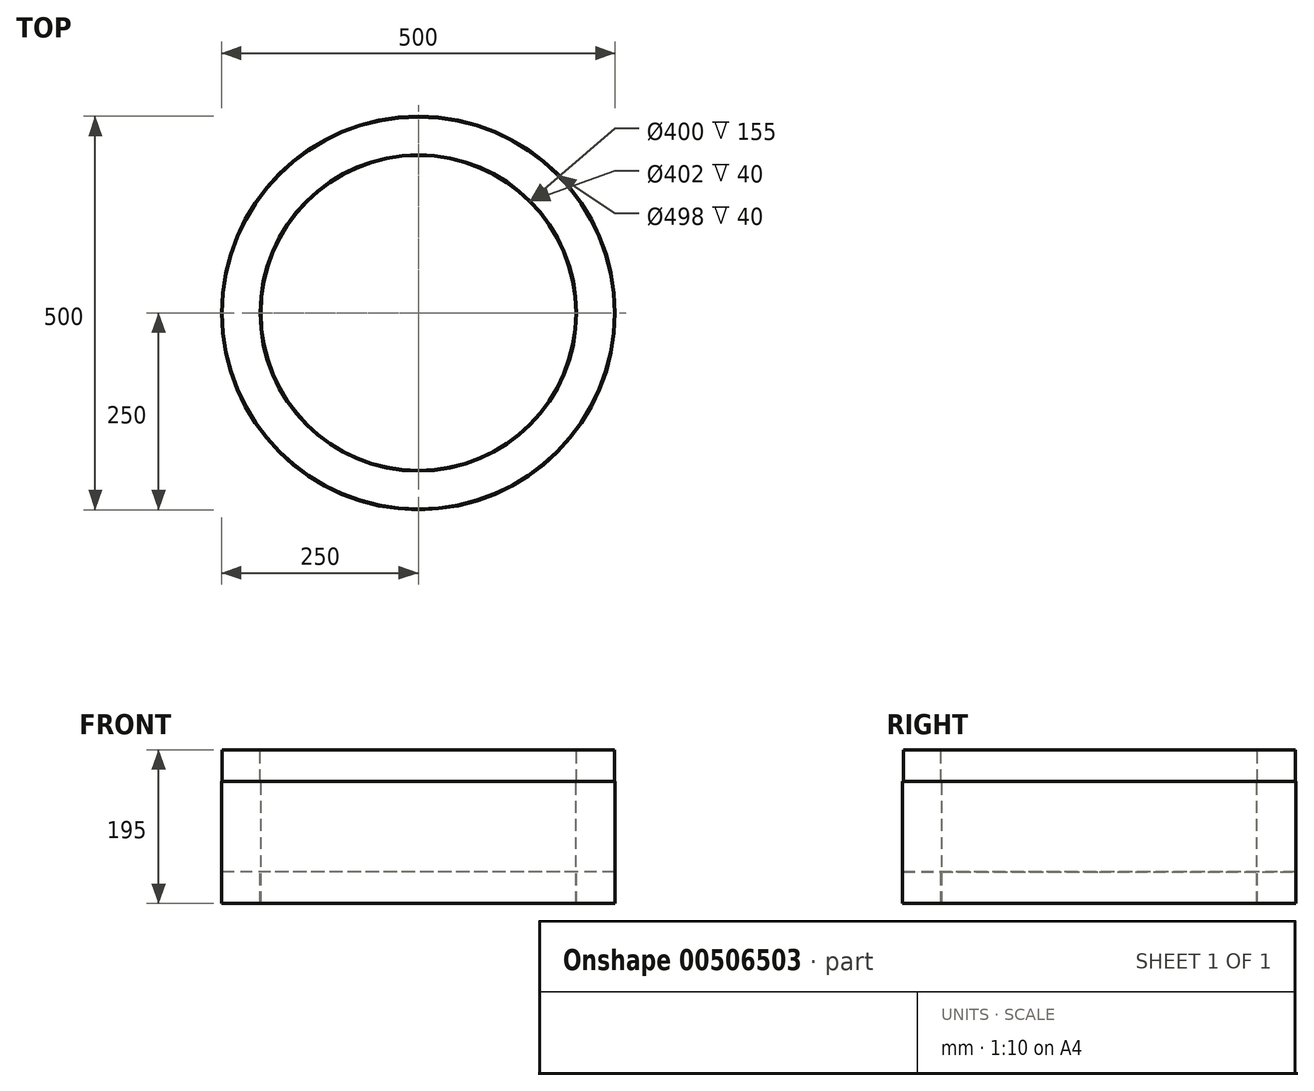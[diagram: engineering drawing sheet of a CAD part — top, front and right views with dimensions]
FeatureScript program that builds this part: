
annotation { "Feature Type Name" : "Feature", "Feature Type Description" : "" }
export const myFeature = defineFeature(function(context is Context, id is Id, definition is map)
    precondition{}
    {
        {
            var Q0;
            Q0=qCreatedBy(makeId("Front.planeOp"),FACE);
            var sketch = newSketch(context, id + "F0", { "sketchPlane" : qUnion([Q0])});
            skLineSegment(sketch, "E0", {"start": v(0, 74.87) * mm, "end": v(0, -73.71) * mm, "construction": true});
            skLineSegment(sketch, "E1", {"start": v(0, 374.84) * mm, "end": v(0, -528.94) * mm, "construction": true});
            skLineSegment(sketch, "E2", {"start": v(-200, -489.75) * mm, "end": v(-200, -334.75) * mm});
            skLineSegment(sketch, "E3", {"start": v(-200, -334.75) * mm, "end": v(-201, -334.75) * mm});
            skLineSegment(sketch, "E4", {"start": v(-201, -334.75) * mm, "end": v(-201, -294.75) * mm});
            skLineSegment(sketch, "E5", {"start": v(-201, -294.75) * mm, "end": v(-249, -294.75) * mm});
            skLineSegment(sketch, "E6", {"start": v(-249, -294.75) * mm, "end": v(-249, -334.75) * mm});
            skLineSegment(sketch, "E7", {"start": v(-249, -334.75) * mm, "end": v(-250, -334.75) * mm});
            skLineSegment(sketch, "E8", {"start": v(-250, -334.75) * mm, "end": v(-250, -489.75) * mm});
            skLineSegment(sketch, "E9", {"start": v(-250, -489.75) * mm, "end": v(-249, -489.75) * mm});
            skLineSegment(sketch, "E10", {"start": v(-249, -489.75) * mm, "end": v(-249, -449.75) * mm});
            skLineSegment(sketch, "E11", {"start": v(-249, -449.75) * mm, "end": v(-201, -449.75) * mm});
            skLineSegment(sketch, "E12", {"start": v(-201, -449.75) * mm, "end": v(-201, -489.75) * mm});
            skLineSegment(sketch, "E13", {"start": v(-201, -489.75) * mm, "end": v(-200, -489.75) * mm});
            skSolve(sketch);
        }
        {
            var Q0;
            Q0=qSketchRegion(id+"F0",true);
            var Q1;
            Q1=sQuery(id+"F0.wireOp",EDGE,"E1");
            revolve(context, id + "F1", {"entities" : qUnion([Q0]), "axis" : qUnion([Q1]), "revolveType" : RevolveType.FULL});
        }
    });
